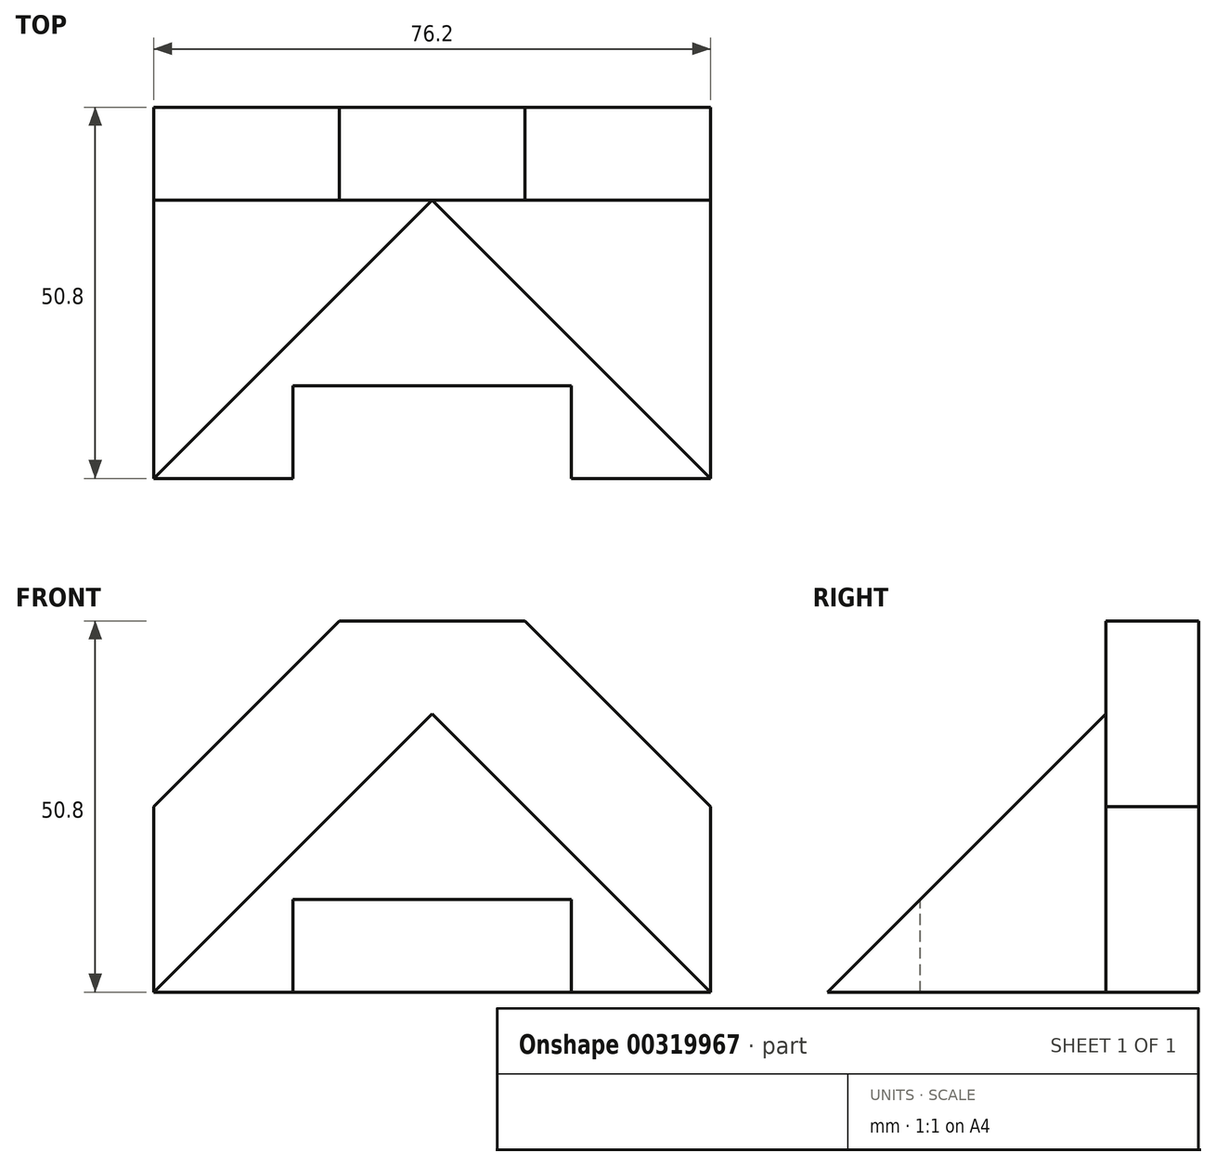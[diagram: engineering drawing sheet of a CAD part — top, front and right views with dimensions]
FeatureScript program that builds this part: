
annotation { "Feature Type Name" : "Feature", "Feature Type Description" : "" }
export const myFeature = defineFeature(function(context is Context, id is Id, definition is map)
    precondition{}
    {
        {
            var Q0;
            Q0=qCreatedBy(makeId("Top.planeOp"),FACE);
            var sketch = newSketch(context, id + "F0", { "sketchPlane" : qUnion([Q0])});
            skLineSegment(sketch, "E0", {"start": v(0, 0) * mm, "end": v(0, 50.8) * mm});
            skLineSegment(sketch, "E1", {"start": v(0, 50.8) * mm, "end": v(76.2, 50.8) * mm});
            skLineSegment(sketch, "E2", {"start": v(76.2, 50.8) * mm, "end": v(76.2, 0) * mm});
            skLineSegment(sketch, "E3", {"start": v(76.2, 0) * mm, "end": v(0, 0) * mm});
            skLineSegment(sketch, "E4", {"start": v(0, 38.1) * mm, "end": v(76.2, 38.1) * mm});
            skLineSegment(sketch, "E5", {"start": v(38.1, 38.1) * mm, "end": v(76.2, 0) * mm});
            skLineSegment(sketch, "E6", {"start": v(38.1, 38.1) * mm, "end": v(0, 0) * mm});
            skLineSegment(sketch, "E7", {"start": v(25.4, 50.8) * mm, "end": v(25.4, 38.1) * mm});
            skLineSegment(sketch, "E8", {"start": v(50.8, 50.8) * mm, "end": v(50.8, 38.1) * mm});
            skLineSegment(sketch, "E9", {"start": v(19.05, 0) * mm, "end": v(19.05, 12.7) * mm});
            skLineSegment(sketch, "E10", {"start": v(19.05, 12.7) * mm, "end": v(57.15, 12.7) * mm});
            skLineSegment(sketch, "E11", {"start": v(57.15, 12.7) * mm, "end": v(57.15, 0) * mm});
            skSolve(sketch);
        }
        {
            var Q0;
            {var subQ3=sQuery(id+"F0.wireOp",EDGE,"E7");Q0=makeQuery(id+"F0.imprint","IMPRINT",FACE,{"disambiguationData":[TD([[makeQuery(id+"F0.imprint","IMPRINT",EDGE,{"derivedFrom":subQ3}),1.0]])]});}
            extrude(context, id + "F1", {"entities" : qUnion([Q0]), "depth" : 50.8 * mm});
        }
        {
            var Q0;
            {var subQ3=sQuery(id+"F0.wireOp",EDGE,"E8");Q0=makeQuery(id+"F0.imprint","IMPRINT",FACE,{"disambiguationData":[TD([[makeQuery(id+"F0.imprint","IMPRINT",EDGE,{"derivedFrom":subQ3}),1.0]])]});}
            var Q1;
            {var subQ5=sQuery(id+"F0.wireOp",EDGE,"E7");Q1=makeQuery(id+"F0.imprint","IMPRINT",FACE,{"disambiguationData":[TD([[makeQuery(id+"F0.imprint","IMPRINT",EDGE,{"derivedFrom":subQ5}),-1.0]])]});}
            extrude(context, id + "F2", {"entities" : qUnion([Q0, Q1]), "operationType" : NewBodyOperationType.ADD, "depth" : 25.4 * mm});
        }
        {
            var Q0;
            {var subQ0=sQuery(id+"F0.wireOp",EDGE,"E1");Q0=makeQuery(id+"F2.boolean.opBoolean","MERGE",FACE,{"derivedFrom":[makeQuery(id+"F1.opExtrude","SWEPT_FACE",FACE,{"disambiguationData":[OSD([subQ0])]}),makeQuery(id+"F2.opExtrude","SWEPT_FACE",FACE,{"disambiguationData":[OSD([subQ0]),TDD([makeQuery(id+"F0.imprint","IMPRINT",EDGE,{"disambiguationData":[TD([[makeQuery(id+"F0.imprint","INTERSECT",VERTEX,{"derivedFrom":[sQuery(id+"F0.wireOp",EDGE,"E0"),subQ0]}),-1.0]])],"derivedFrom":subQ0})])]}),makeQuery(id+"F2.opExtrude","SWEPT_FACE",FACE,{"disambiguationData":[OSD([subQ0]),TDD([makeQuery(id+"F0.imprint","IMPRINT",EDGE,{"disambiguationData":[TD([[makeQuery(id+"F0.imprint","INTERSECT",VERTEX,{"derivedFrom":[subQ0,sQuery(id+"F0.wireOp",EDGE,"E2")]}),1.0]])],"derivedFrom":subQ0})])]})]});}
            var sketch = newSketch(context, id + "F3", { "sketchPlane" : qUnion([Q0])});
            skLineSegment(sketch, "E12", {"start": v(-25.4, 50.8) * mm, "end": v(0, 25.4) * mm});
            skLineSegment(sketch, "E13", {"start": v(-50.8, 50.8) * mm, "end": v(-76.2, 25.4) * mm});
            skSolve(sketch);
        }
        {
            var Q0;
            Q0=makeQuery(id+"F3.imprint","IMPRINT",FACE,{"disambiguationData":[TD([[makeQuery(id+"F3.imprint","IMPRINT",EDGE,{"derivedFrom":sQuery(id+"F3.wireOp",EDGE,"E13")}),1.0]])]});
            var Q1;
            Q1=makeQuery(id+"F3.imprint","IMPRINT",FACE,{"disambiguationData":[TD([[makeQuery(id+"F3.imprint","IMPRINT",EDGE,{"derivedFrom":sQuery(id+"F3.wireOp",EDGE,"E12")}),-1.0]])]});
            extrude(context, id + "F4", {"entities" : qUnion([Q0, Q1]), "operationType" : NewBodyOperationType.ADD, "oppositeDirection" : true, "depth" : 12.7 * mm});
        }
        {
            var Q0;
            {var subQ0=sQuery(id+"F0.wireOp",EDGE,"E8");var subQ1=sQuery(id+"F0.wireOp",EDGE,"E1");var subQ2=sQuery(id+"F0.wireOp",EDGE,"E7");var subQ3=sQuery(id+"F0.wireOp",EDGE,"E4");Q0=makeQuery(id+"F4.boolean.opBoolean","MERGE",FACE,{"derivedFrom":[makeQuery(id+"F2.boolean.opBoolean","MERGE",FACE,{"derivedFrom":[makeQuery(id+"F1.opExtrude","SWEPT_FACE",FACE,{"disambiguationData":[OSD([subQ3])]}),makeQuery(id+"F2.opExtrude","SWEPT_FACE",FACE,{"disambiguationData":[OSD([subQ3]),TDD([makeQuery(id+"F0.imprint","IMPRINT",EDGE,{"disambiguationData":[TD([[makeQuery(id+"F0.imprint","INTERSECT",VERTEX,{"derivedFrom":[sQuery(id+"F0.wireOp",EDGE,"E0"),subQ3]}),-1.0]])],"derivedFrom":subQ3})])]}),makeQuery(id+"F2.opExtrude","SWEPT_FACE",FACE,{"disambiguationData":[OSD([subQ3]),TDD([makeQuery(id+"F0.imprint","IMPRINT",EDGE,{"disambiguationData":[TD([[makeQuery(id+"F0.imprint","INTERSECT",VERTEX,{"derivedFrom":[sQuery(id+"F0.wireOp",EDGE,"E2"),subQ3]}),1.0]])],"derivedFrom":subQ3})])]})]}),makeQuery(id+"F4.opExtrude","CAP_FACE",FACE,{"disambiguationData":[OSD([subQ1,subQ2,sQuery(id+"F3.wireOp",EDGE,"E12")])],"isStart":false}),makeQuery(id+"F4.opExtrude","CAP_FACE",FACE,{"disambiguationData":[OSD([subQ1,subQ0,sQuery(id+"F3.wireOp",EDGE,"E13")])],"isStart":false})]});}
            var sketch = newSketch(context, id + "F5", { "sketchPlane" : qUnion([Q0])});
            skLineSegment(sketch, "E14", {"start": v(38.1, 38.1) * mm, "end": v(76.2, 0) * mm});
            skPoint(sketch, "E14.startSnap0", {"position": v(38.1, 50.8) * mm});
            skLineSegment(sketch, "E15", {"start": v(76.2, 0) * mm, "end": v(0, 0) * mm});
            skLineSegment(sketch, "E16", {"start": v(0, 0) * mm, "end": v(38.1, 38.1) * mm});
            skPoint(sketch, "E17.0", {"position": v(19.05, 0) * mm});
            skPoint(sketch, "E18.0", {"position": v(57.15, 0) * mm});
            skLineSegment(sketch, "E19", {"start": v(19.05, 0) * mm, "end": v(19.05, 12.7) * mm});
            skLineSegment(sketch, "E20", {"start": v(19.05, 12.7) * mm, "end": v(57.15, 12.7) * mm});
            skLineSegment(sketch, "E21", {"start": v(57.15, 12.7) * mm, "end": v(57.15, 0) * mm});
            skSolve(sketch);
        }
        {
            var Q0;
            {var subQ2=sQuery(id+"F5.wireOp",EDGE,"E14");Q0=makeQuery(id+"F5.imprint","IMPRINT",FACE,{"disambiguationData":[TD([[makeQuery(id+"F5.imprint","IMPRINT",EDGE,{"derivedFrom":subQ2}),-1.0]])]});}
            extrude(context, id + "F6", {"entities" : qUnion([Q0]), "operationType" : NewBodyOperationType.ADD, "depth" : 38.1 * mm});
        }
        {
            var Q0;
            {var subQ1=sQuery(id+"F0.wireOp",EDGE,"E4");var subQ2=sQuery(id+"F0.wireOp",EDGE,"E0");var subQ3=sQuery(id+"F5.wireOp",EDGE,"E19");var subQ4=sQuery(id+"F0.wireOp",EDGE,"E7");var subQ5=sQuery(id+"F0.wireOp",EDGE,"E1");var subQ6=sQuery(id+"F0.wireOp",EDGE,"E8");var subQ7=sQuery(id+"F0.wireOp",EDGE,"E2");Q0=makeQuery(id+"F6.boolean.opBoolean","SPLIT",FACE,{"disambiguationData":[TD([makeQuery(id+"F6.opExtrude","SWEPT_FACE",FACE,{"disambiguationData":[OSD([subQ3])]})])],"derivedFrom":makeQuery(id+"F4.boolean.opBoolean","MERGE",FACE,{"derivedFrom":[makeQuery(id+"F2.boolean.opBoolean","MERGE",FACE,{"derivedFrom":[makeQuery(id+"F1.opExtrude","SWEPT_FACE",FACE,{"disambiguationData":[OSD([subQ1])]}),makeQuery(id+"F2.opExtrude","SWEPT_FACE",FACE,{"disambiguationData":[OSD([subQ1]),TDD([makeQuery(id+"F0.imprint","IMPRINT",EDGE,{"disambiguationData":[TD([[makeQuery(id+"F0.imprint","INTERSECT",VERTEX,{"derivedFrom":[subQ2,subQ1]}),-1.0]])],"derivedFrom":subQ1})])]}),makeQuery(id+"F2.opExtrude","SWEPT_FACE",FACE,{"disambiguationData":[OSD([subQ1]),TDD([makeQuery(id+"F0.imprint","IMPRINT",EDGE,{"disambiguationData":[TD([[makeQuery(id+"F0.imprint","INTERSECT",VERTEX,{"derivedFrom":[subQ7,subQ1]}),1.0]])],"derivedFrom":subQ1})])]})]}),makeQuery(id+"F4.opExtrude","CAP_FACE",FACE,{"disambiguationData":[OSD([subQ5,subQ4,sQuery(id+"F3.wireOp",EDGE,"E12")])],"isStart":false}),makeQuery(id+"F4.opExtrude","CAP_FACE",FACE,{"disambiguationData":[OSD([subQ5,subQ6,sQuery(id+"F3.wireOp",EDGE,"E13")])],"isStart":false})]})});}
            extrude(context, id + "F7", {"entities" : qUnion([Q0]), "operationType" : NewBodyOperationType.ADD, "depth" : 25.4 * mm});
        }
        {
            var Q0;
            Q0=makeQuery(id+"F2.opExtrude","SWEPT_FACE",FACE,{"disambiguationData":[OSD([sQuery(id+"F0.wireOp",EDGE,"E2")])]});
            var sketch = newSketch(context, id + "F8", { "sketchPlane" : qUnion([Q0])});
            skPoint(sketch, "E22.0", {"position": v(38.1, 38.1) * mm});
            skPoint(sketch, "E23.0", {"position": v(0, 38.1) * mm});
            skLineSegment(sketch, "E24", {"start": v(0, 38.1) * mm, "end": v(38.1, 38.1) * mm});
            skLineSegment(sketch, "E25", {"start": v(0, 0) * mm, "end": v(38.1, 38.1) * mm});
            skLineSegment(sketch, "E26", {"start": v(0, 38.1) * mm, "end": v(0, 0) * mm});
            skSolve(sketch);
        }
        {
            var Q0;
            Q0 = qSketchRegion(id + "F8", true);
            extrude(context, id + "F9", {"entities" : qUnion([Q0]), "operationType" : NewBodyOperationType.REMOVE, "endBound" : BoundingType.THROUGH_ALL, "oppositeDirection" : true, "depth" : 25.4 * mm});
        }
    });
